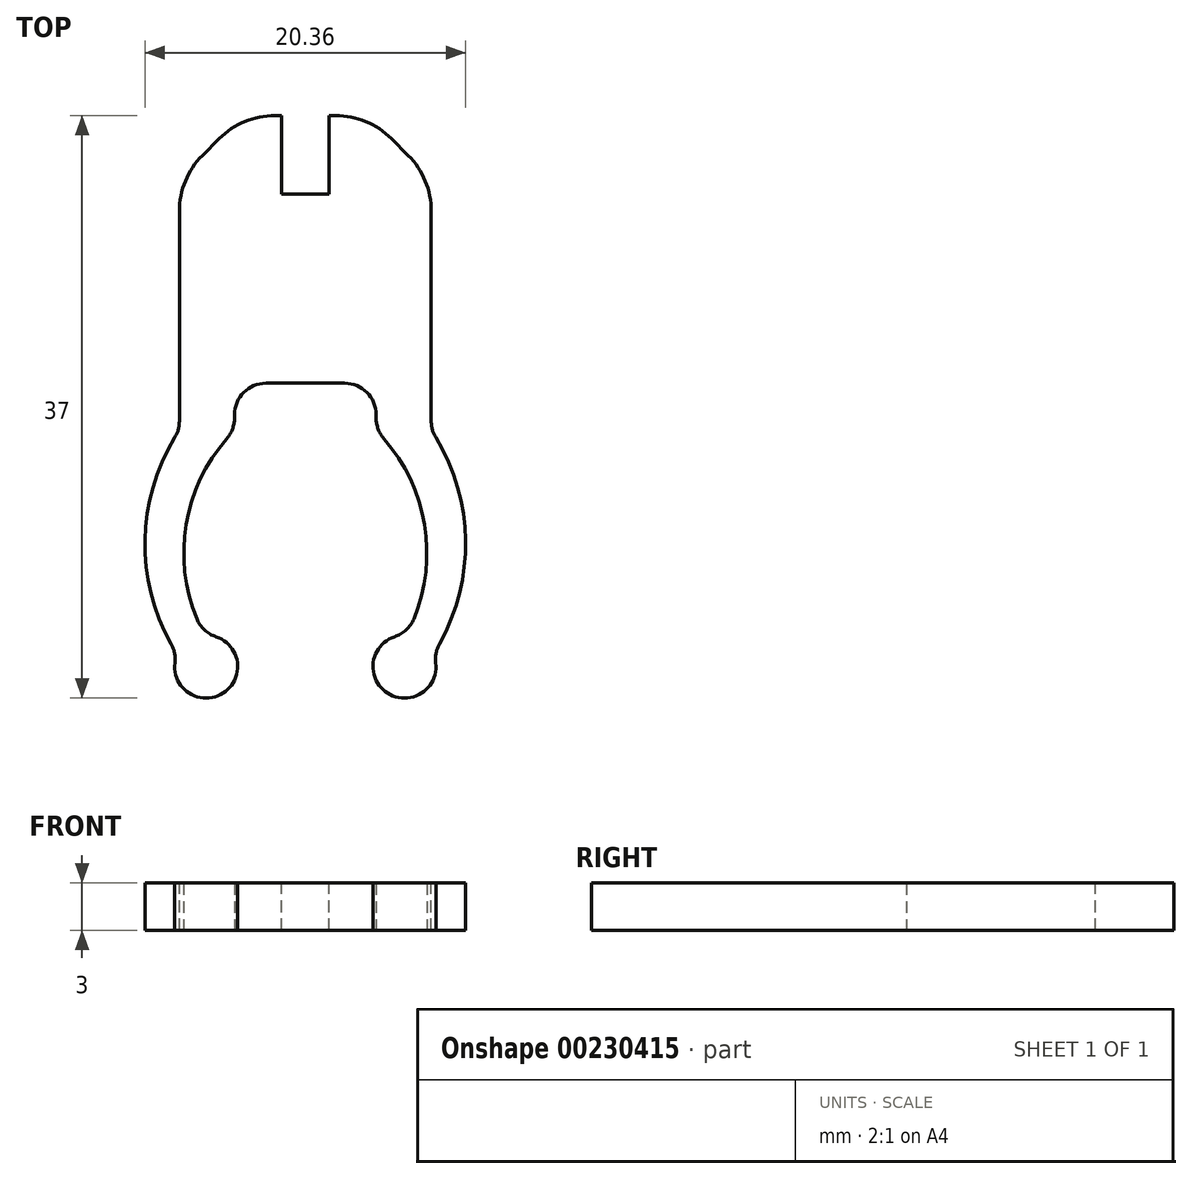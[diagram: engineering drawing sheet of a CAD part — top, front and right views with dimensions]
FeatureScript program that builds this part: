
annotation { "Feature Type Name" : "Feature", "Feature Type Description" : "" }
export const myFeature = defineFeature(function(context is Context, id is Id, definition is map)
    precondition{}
    {
        {
            var Q0;
            Q0=qCreatedBy(makeId("Top.planeOp"),FACE);
            var sketch = newSketch(context, id + "F0", { "sketchPlane" : qUnion([Q0])});
            skSolve(sketch);
        }
        {
            var Q0;
            Q0=qCreatedBy(makeId("Top.planeOp"),FACE);
            var sketch = newSketch(context, id + "F1", { "sketchPlane" : qUnion([Q0])});
            skLineSegment(sketch, "E0.bottom", {"start": v(25, -9) * mm, "end": v(41, -9) * mm});
            skLineSegment(sketch, "E0.top", {"start": v(25, -29) * mm, "end": v(41, -29) * mm});
            skLineSegment(sketch, "E0.left", {"start": v(25, -9) * mm, "end": v(25, -29) * mm});
            skLineSegment(sketch, "E0.right", {"start": v(41, -9) * mm, "end": v(41, -29) * mm});
            skLineSegment(sketch, "E1.bottom", {"start": v(28.5, -29) * mm, "end": v(37.5, -29) * mm});
            skLineSegment(sketch, "E1.top", {"start": v(28.5, -26) * mm, "end": v(37.5, -26) * mm});
            skLineSegment(sketch, "E1.left", {"start": v(28.5, -29) * mm, "end": v(28.5, -26) * mm});
            skLineSegment(sketch, "E1.right", {"start": v(37.5, -29) * mm, "end": v(37.5, -26) * mm});
            skCircle(sketch, "E2", {"center": v(26.7, -44) * mm, "radius": 2 * mm});
            skCircle(sketch, "E3", {"center": v(26.7, -44) * mm, "radius": 1 * mm});
            skArc(sketch, "E4", {"start": v(25, -29) * mm, "mid": v(22.85, -36.98) * mm, "end": v(25.94, -44.65) * mm});
            skArc(sketch, "E5", {"start": v(28.5, -29) * mm, "mid": v(25.3, -36.01) * mm, "end": v(27.5, -43.4) * mm});
            skLineSegment(sketch, "E6", {"start": v(33, -9) * mm, "end": v(33, -43.66) * mm});
            skSolve(sketch);
        }
        {
            var Q0;
            {var subQ0=sQuery(id+"F1.wireOp",EDGE,"E4");var subQ1=sQuery(id+"F1.wireOp",EDGE,"E2");var subQ2=makeQuery(id+"F1.imprint","INTERSECT",VERTEX,{"derivedFrom":[subQ1,subQ0]});Q0=makeQuery(id+"F1.imprint","IMPRINT",FACE,{"disambiguationData":[TD([[makeQuery(id+"F1.imprint","IMPRINT",EDGE,{"disambiguationData":[TD([[subQ2,-1.0]])],"derivedFrom":subQ1}),1.0]])]});}
            var Q1;
            {var subQ0=sQuery(id+"F1.wireOp",EDGE,"E3");var subQ1=makeQuery(id+"F1.imprint","INTERSECT",VERTEX,{"derivedFrom":[subQ0,sQuery(id+"F1.wireOp",EDGE,"E4")]});Q1=makeQuery(id+"F1.imprint","IMPRINT",FACE,{"disambiguationData":[TD([[makeQuery(id+"F1.imprint","IMPRINT",EDGE,{"disambiguationData":[TD([[subQ1,1.0]])],"derivedFrom":subQ0}),1.0]])]});}
            var Q2;
            {var subQ0=sQuery(id+"F1.wireOp",EDGE,"E4");var subQ1=sQuery(id+"F1.wireOp",EDGE,"E2");var subQ2=makeQuery(id+"F1.imprint","INTERSECT",VERTEX,{"derivedFrom":[subQ1,subQ0]});Q2=makeQuery(id+"F1.imprint","IMPRINT",FACE,{"disambiguationData":[TD([[makeQuery(id+"F1.imprint","IMPRINT",EDGE,{"disambiguationData":[TD([[subQ2,1.0]])],"derivedFrom":subQ1}),1.0]])]});}
            var Q3;
            {var subQ0=sQuery(id+"F1.wireOp",EDGE,"E4");var subQ5=sQuery(id+"F1.wireOp",EDGE,"E2");var subQ6=makeQuery(id+"F1.imprint","INTERSECT",VERTEX,{"derivedFrom":[subQ5,subQ0]});Q3=makeQuery(id+"F1.imprint","IMPRINT",FACE,{"disambiguationData":[TD([[makeQuery(id+"F1.imprint","IMPRINT",EDGE,{"disambiguationData":[TD([[subQ6,1.0]])],"derivedFrom":subQ5}),-1.0]])]});}
            var Q4;
            {var subQ6=sQuery(id+"F1.wireOp",EDGE,"E0.left");Q4=makeQuery(id+"F1.imprint","IMPRINT",FACE,{"disambiguationData":[TD([[makeQuery(id+"F1.imprint","IMPRINT",EDGE,{"derivedFrom":subQ6}),1.0]])]});}
            extrude(context, id + "F2", {"entities" : qUnion([Q0, Q1, Q2, Q3, Q4]), "depth" : 3 * mm, "symmetric" : true});
        }
        {
            var Q0;
            Q0=makeQuery(id+"F2.opExtrude","SWEPT_BODY",BODY,{"disambiguationData":[OSD([sQuery(id+"F1.wireOp",EDGE,"E0.bottom"),sQuery(id+"F1.wireOp",EDGE,"E0.left"),sQuery(id+"F1.wireOp",EDGE,"E1.top"),sQuery(id+"F1.wireOp",EDGE,"E1.left"),sQuery(id+"F1.wireOp",EDGE,"E2"),sQuery(id+"F1.wireOp",EDGE,"E4"),sQuery(id+"F1.wireOp",EDGE,"E5"),sQuery(id+"F1.wireOp",EDGE,"E6")])]});
            transform(context, id + "F3", {"entities" : qUnion([Q0]), "transformType" : TransformType.TRANSLATION_3D, "dx" : -33 * mm, "dy" : 26 * mm, "dz" : 0 * mm, "makeCopy" : false});
        }
        {
            var Q0;
            Q0=makeQuery(id+"F2.opExtrude","SWEPT_BODY",BODY,{"disambiguationData":[OSD([sQuery(id+"F1.wireOp",EDGE,"E0.bottom"),sQuery(id+"F1.wireOp",EDGE,"E0.left"),sQuery(id+"F1.wireOp",EDGE,"E1.top"),sQuery(id+"F1.wireOp",EDGE,"E1.left"),sQuery(id+"F1.wireOp",EDGE,"E2"),sQuery(id+"F1.wireOp",EDGE,"E4"),sQuery(id+"F1.wireOp",EDGE,"E5"),sQuery(id+"F1.wireOp",EDGE,"E6")])]});
            var Q1;
            Q1=qCreatedBy(makeId("Right.planeOp"),FACE);
            mirror(context, id + "F4", {"operationType" : NewBodyOperationType.ADD, "entities" : qUnion([Q0]), "mirrorPlane" : qUnion([Q1])});
        }
        {
            var Q0;
            {var subQ0=makeQuery(id+"F2.opExtrude","CAP_FACE",FACE,{"disambiguationData":[OSD([sQuery(id+"F1.wireOp",EDGE,"E0.bottom"),sQuery(id+"F1.wireOp",EDGE,"E0.left"),sQuery(id+"F1.wireOp",EDGE,"E1.top"),sQuery(id+"F1.wireOp",EDGE,"E1.left"),sQuery(id+"F1.wireOp",EDGE,"E2"),sQuery(id+"F1.wireOp",EDGE,"E4"),sQuery(id+"F1.wireOp",EDGE,"E5"),sQuery(id+"F1.wireOp",EDGE,"E6")])],"isStart":false});Q0=makeQuery(id+"F4.boolean.opBoolean","MERGE",FACE,{"derivedFrom":[subQ0,makeQuery(id+"F4.opPattern","COPY",FACE,{"derivedFrom":subQ0,"instanceName":"1"})]});}
            var sketch = newSketch(context, id + "F5", { "sketchPlane" : qUnion([Q0])});
            skLineSegment(sketch, "E7.bottom", {"start": v(-1.5, 17) * mm, "end": v(1.5, 17) * mm});
            skLineSegment(sketch, "E7.top", {"start": v(-1.5, 12) * mm, "end": v(1.5, 12) * mm});
            skLineSegment(sketch, "E7.left", {"start": v(-1.5, 17) * mm, "end": v(-1.5, 12) * mm});
            skLineSegment(sketch, "E7.right", {"start": v(1.5, 17) * mm, "end": v(1.5, 12) * mm});
            skPoint(sketch, "E8", {"position": v(0, 12) * mm});
            skSolve(sketch);
        }
        {
            var Q0;
            Q0 = qSketchRegion(id + "F5", true);
            extrude(context, id + "F6", {"entities" : qUnion([Q0]), "operationType" : NewBodyOperationType.REMOVE, "oppositeDirection" : true, "depth" : 25 * mm});
        }
        {
            var Q0;
            Q0=makeQuery(id+"F2.opExtrude","SWEPT_EDGE",EDGE,{"disambiguationData":[OSD([sQuery(id+"F1.wireOp",EDGE,"E0.bottom"),sQuery(id+"F1.wireOp",EDGE,"E0.left")])]});
            var Q1;
            Q1=makeQuery(id+"F4.opPattern","COPY",EDGE,{"derivedFrom":makeQuery(id+"F2.opExtrude","SWEPT_EDGE",EDGE,{"disambiguationData":[OSD([sQuery(id+"F1.wireOp",EDGE,"E0.bottom"),sQuery(id+"F1.wireOp",EDGE,"E0.left")])]}),"instanceName":"1"});
            chamfer(context, id + "F7", {"entities" : qUnion([Q0, Q1]), "width" : 4 * mm, "tangentPropagation" : true});
        }
        {
            var Q0;
            {var subQ0=sQuery(id+"F1.wireOp",EDGE,"E0.left");Q0=makeQuery(id+"F7.opChamfer","BLEND_EDGE",EDGE,{"blendedFrom":[makeQuery(id+"F2.opExtrude","SWEPT_EDGE",EDGE,{"disambiguationData":[OSD([sQuery(id+"F1.wireOp",EDGE,"E0.bottom"),subQ0])]}),makeQuery(id+"F2.opExtrude","SWEPT_FACE",FACE,{"disambiguationData":[OSD([subQ0])]})],"blendedInto":[makeQuery(id+"F2.opExtrude","SWEPT_FACE",FACE,{"disambiguationData":[OSD([subQ0])]})]});}
            var Q1;
            {var subQ6=sQuery(id+"F1.wireOp",EDGE,"E0.left");var subQ7=sQuery(id+"F1.wireOp",EDGE,"E0.bottom");var subQ10=makeQuery(id+"F2.opExtrude","SWEPT_FACE",FACE,{"disambiguationData":[OSD([subQ7])]});Q1=makeQuery(id+"F7.opChamfer","BLEND_EDGE",EDGE,{"blendedFrom":[makeQuery(id+"F2.opExtrude","SWEPT_EDGE",EDGE,{"disambiguationData":[OSD([subQ7,subQ6])]}),makeQuery(id+"F6.boolean.opBoolean","SPLIT",FACE,{"disambiguationData":[TD([makeQuery(id+"F2.opExtrude","SWEPT_FACE",FACE,{"disambiguationData":[OSD([subQ6])]})])],"derivedFrom":makeQuery(id+"F4.boolean.opBoolean","MERGE",FACE,{"derivedFrom":[subQ10,makeQuery(id+"F4.opPattern","COPY",FACE,{"derivedFrom":subQ10,"instanceName":"1"})]})})],"blendedInto":[makeQuery(id+"F6.boolean.opBoolean","SPLIT",FACE,{"disambiguationData":[TD([makeQuery(id+"F2.opExtrude","SWEPT_FACE",FACE,{"disambiguationData":[OSD([subQ6])]})])],"derivedFrom":makeQuery(id+"F4.boolean.opBoolean","MERGE",FACE,{"derivedFrom":[subQ10,makeQuery(id+"F4.opPattern","COPY",FACE,{"derivedFrom":subQ10,"instanceName":"1"})]})})]});}
            var Q2;
            {var subQ6=sQuery(id+"F1.wireOp",EDGE,"E0.left");var subQ7=sQuery(id+"F1.wireOp",EDGE,"E0.bottom");var subQ10=makeQuery(id+"F2.opExtrude","SWEPT_FACE",FACE,{"disambiguationData":[OSD([subQ7])]});Q2=makeQuery(id+"F7.opChamfer","BLEND_EDGE",EDGE,{"blendedFrom":[makeQuery(id+"F4.opPattern","COPY",EDGE,{"derivedFrom":makeQuery(id+"F2.opExtrude","SWEPT_EDGE",EDGE,{"disambiguationData":[OSD([subQ7,subQ6])]}),"instanceName":"1"}),makeQuery(id+"F6.boolean.opBoolean","SPLIT",FACE,{"disambiguationData":[TD([makeQuery(id+"F4.opPattern","COPY",FACE,{"derivedFrom":makeQuery(id+"F2.opExtrude","SWEPT_FACE",FACE,{"disambiguationData":[OSD([subQ6])]}),"instanceName":"1"})])],"derivedFrom":makeQuery(id+"F4.boolean.opBoolean","MERGE",FACE,{"derivedFrom":[subQ10,makeQuery(id+"F4.opPattern","COPY",FACE,{"derivedFrom":subQ10,"instanceName":"1"})]})})],"blendedInto":[makeQuery(id+"F6.boolean.opBoolean","SPLIT",FACE,{"disambiguationData":[TD([makeQuery(id+"F4.opPattern","COPY",FACE,{"derivedFrom":makeQuery(id+"F2.opExtrude","SWEPT_FACE",FACE,{"disambiguationData":[OSD([subQ6])]}),"instanceName":"1"})])],"derivedFrom":makeQuery(id+"F4.boolean.opBoolean","MERGE",FACE,{"derivedFrom":[subQ10,makeQuery(id+"F4.opPattern","COPY",FACE,{"derivedFrom":subQ10,"instanceName":"1"})]})})]});}
            var Q3;
            {var subQ0=sQuery(id+"F1.wireOp",EDGE,"E0.left");Q3=makeQuery(id+"F7.opChamfer","BLEND_EDGE",EDGE,{"blendedFrom":[makeQuery(id+"F4.opPattern","COPY",EDGE,{"derivedFrom":makeQuery(id+"F2.opExtrude","SWEPT_EDGE",EDGE,{"disambiguationData":[OSD([sQuery(id+"F1.wireOp",EDGE,"E0.bottom"),subQ0])]}),"instanceName":"1"}),makeQuery(id+"F4.opPattern","COPY",FACE,{"derivedFrom":makeQuery(id+"F2.opExtrude","SWEPT_FACE",FACE,{"disambiguationData":[OSD([subQ0])]}),"instanceName":"1"})],"blendedInto":[makeQuery(id+"F4.opPattern","COPY",FACE,{"derivedFrom":makeQuery(id+"F2.opExtrude","SWEPT_FACE",FACE,{"disambiguationData":[OSD([subQ0])]}),"instanceName":"1"})]});}
            fillet(context, id + "F8", {"entities" : qUnion([Q0, Q1, Q2, Q3]), "radius" : 5 * mm, "tangentPropagation" : true, "allowEdgeOverflow" : false});
        }
        {
            var Q0;
            Q0=makeQuery(id+"F2.opExtrude","SWEPT_EDGE",EDGE,{"disambiguationData":[OSD([sQuery(id+"F1.wireOp",EDGE,"E0.top"),sQuery(id+"F1.wireOp",EDGE,"E0.left"),sQuery(id+"F1.wireOp",EDGE,"E4")])]});
            var Q1;
            Q1=makeQuery(id+"F2.opExtrude","SWEPT_EDGE",EDGE,{"disambiguationData":[OSD([sQuery(id+"F1.wireOp",EDGE,"E0.top"),sQuery(id+"F1.wireOp",EDGE,"E1.bottom"),sQuery(id+"F1.wireOp",EDGE,"E1.left"),sQuery(id+"F1.wireOp",EDGE,"E5")])]});
            var Q2;
            Q2=makeQuery(id+"F4.opPattern","COPY",EDGE,{"derivedFrom":makeQuery(id+"F2.opExtrude","SWEPT_EDGE",EDGE,{"disambiguationData":[OSD([sQuery(id+"F1.wireOp",EDGE,"E0.top"),sQuery(id+"F1.wireOp",EDGE,"E1.bottom"),sQuery(id+"F1.wireOp",EDGE,"E1.left"),sQuery(id+"F1.wireOp",EDGE,"E5")])]}),"instanceName":"1"});
            var Q3;
            Q3=makeQuery(id+"F4.opPattern","COPY",EDGE,{"derivedFrom":makeQuery(id+"F2.opExtrude","SWEPT_EDGE",EDGE,{"disambiguationData":[OSD([sQuery(id+"F1.wireOp",EDGE,"E0.top"),sQuery(id+"F1.wireOp",EDGE,"E0.left"),sQuery(id+"F1.wireOp",EDGE,"E4")])]}),"instanceName":"1"});
            var Q4;
            Q4=makeQuery(id+"F2.opExtrude","SWEPT_EDGE",EDGE,{"disambiguationData":[OSD([sQuery(id+"F1.wireOp",EDGE,"E1.top"),sQuery(id+"F1.wireOp",EDGE,"E1.left")])]});
            var Q5;
            Q5=makeQuery(id+"F4.opPattern","COPY",EDGE,{"derivedFrom":makeQuery(id+"F2.opExtrude","SWEPT_EDGE",EDGE,{"disambiguationData":[OSD([sQuery(id+"F1.wireOp",EDGE,"E1.top"),sQuery(id+"F1.wireOp",EDGE,"E1.left")])]}),"instanceName":"1"});
            var Q6;
            Q6=makeQuery(id+"F2.opExtrude","SWEPT_EDGE",EDGE,{"disambiguationData":[OSD([sQuery(id+"F1.wireOp",EDGE,"E2"),sQuery(id+"F1.wireOp",EDGE,"E4")])]});
            var Q7;
            Q7=makeQuery(id+"F2.opExtrude","SWEPT_EDGE",EDGE,{"disambiguationData":[OSD([sQuery(id+"F1.wireOp",EDGE,"E2"),sQuery(id+"F1.wireOp",EDGE,"E5")])]});
            var Q8;
            Q8=makeQuery(id+"F4.opPattern","COPY",EDGE,{"derivedFrom":makeQuery(id+"F2.opExtrude","SWEPT_EDGE",EDGE,{"disambiguationData":[OSD([sQuery(id+"F1.wireOp",EDGE,"E2"),sQuery(id+"F1.wireOp",EDGE,"E4")])]}),"instanceName":"1"});
            var Q9;
            Q9=makeQuery(id+"F4.opPattern","COPY",EDGE,{"derivedFrom":makeQuery(id+"F2.opExtrude","SWEPT_EDGE",EDGE,{"disambiguationData":[OSD([sQuery(id+"F1.wireOp",EDGE,"E2"),sQuery(id+"F1.wireOp",EDGE,"E5")])]}),"instanceName":"1"});
            fillet(context, id + "F9", {"entities" : qUnion([Q0, Q1, Q2, Q3, Q4, Q5, Q6, Q7, Q8, Q9]), "radius" : 2 * mm, "tangentPropagation" : true, "allowEdgeOverflow" : false});
        }
    });
